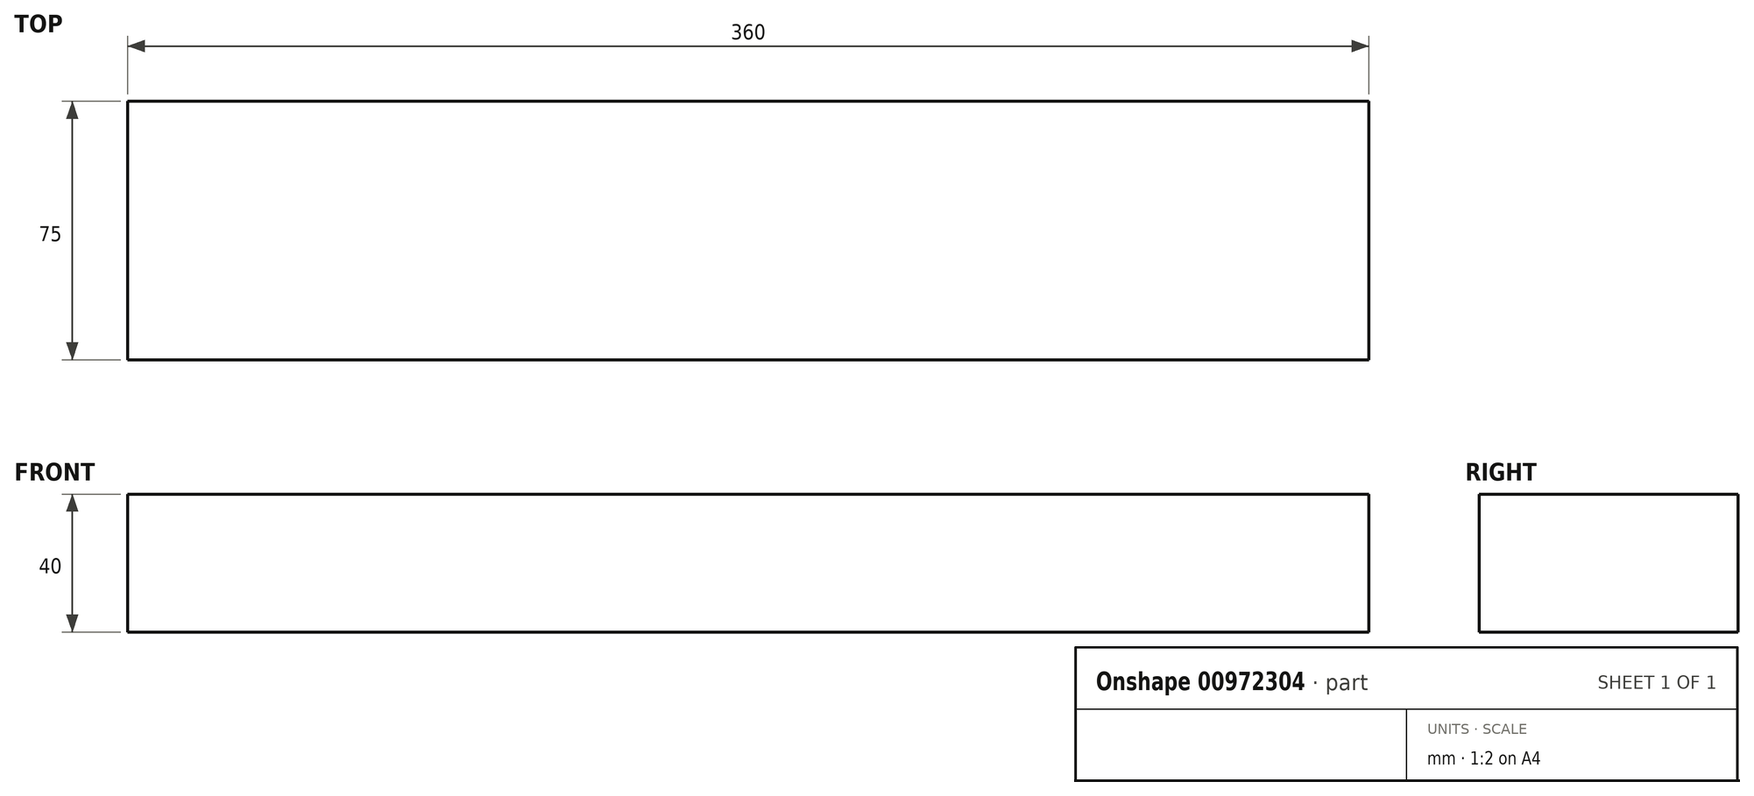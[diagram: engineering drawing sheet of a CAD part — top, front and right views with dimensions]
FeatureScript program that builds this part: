
annotation { "Feature Type Name" : "Feature", "Feature Type Description" : "" }
export const myFeature = defineFeature(function(context is Context, id is Id, definition is map)
    precondition{}
    {
        {
            var Q0;
            Q0=qCreatedBy(makeId("Top.planeOp"),FACE);
            var sketch = newSketch(context, id + "F0", { "sketchPlane" : qUnion([Q0])});
            skLineSegment(sketch, "E0.bottom", {"start": v(-142.34, 36.7) * mm, "end": v(217.66, 36.7) * mm});
            skLineSegment(sketch, "E0.top", {"start": v(-142.34, -38.3) * mm, "end": v(217.66, -38.3) * mm});
            skLineSegment(sketch, "E0.left", {"start": v(-142.34, 36.7) * mm, "end": v(-142.34, -38.3) * mm});
            skLineSegment(sketch, "E0.right", {"start": v(217.66, 36.7) * mm, "end": v(217.66, -38.3) * mm});
            skSolve(sketch);
        }
        {
            var Q0;
            Q0=makeQuery(id+"F0.imprint","IMPRINT",FACE,{"disambiguationData":[TD([[makeQuery(id+"F0.imprint","IMPRINT",EDGE,{"derivedFrom":sQuery(id+"F0.wireOp",EDGE,"E0.bottom")}),-1.0]])]});
            extrude(context, id + "F1", {"entities" : qUnion([Q0]), "depth" : 40 * mm, "offsetDistance" : 25 * mm});
        }
    });
